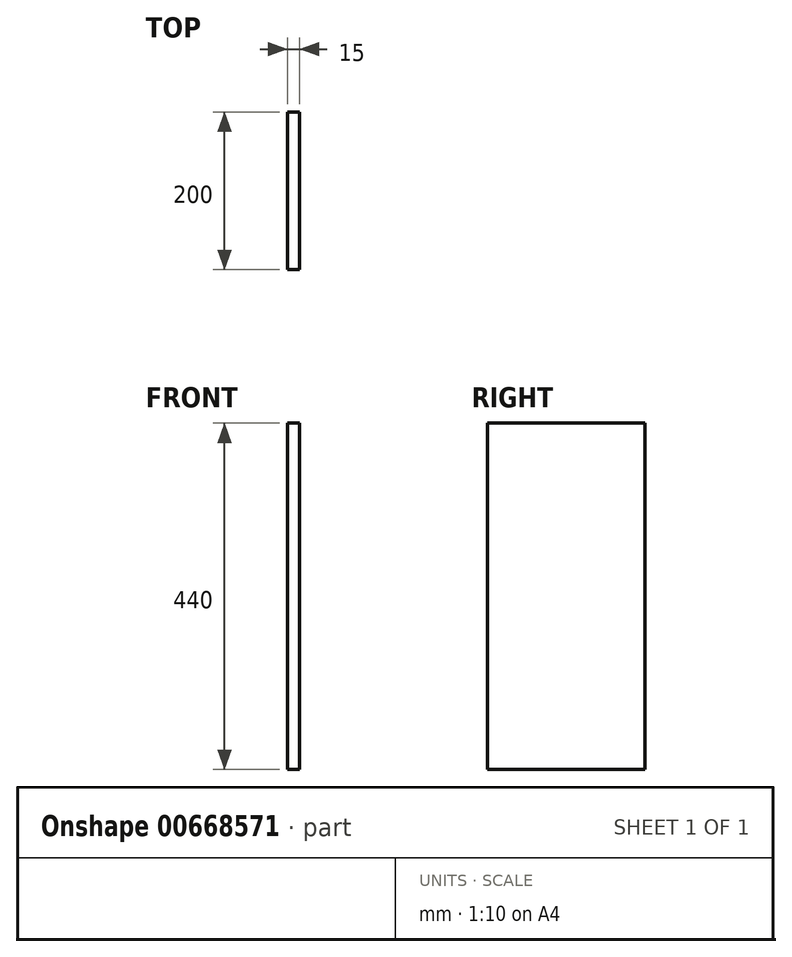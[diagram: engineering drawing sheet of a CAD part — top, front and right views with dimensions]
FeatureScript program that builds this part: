
annotation { "Feature Type Name" : "Feature", "Feature Type Description" : "" }
export const myFeature = defineFeature(function(context is Context, id is Id, definition is map)
    precondition{}
    {
        {
            var Q0;
            Q0=qCreatedBy(makeId("Right.planeOp"),FACE);
            var sketch = newSketch(context, id + "F0", { "sketchPlane" : qUnion([Q0])});
            skLineSegment(sketch, "E0.bottom", {"start": v(0, 0) * mm, "end": v(200, 0) * mm});
            skLineSegment(sketch, "E0.top", {"start": v(0, 440) * mm, "end": v(200, 440) * mm});
            skLineSegment(sketch, "E0.left", {"start": v(0, 0) * mm, "end": v(0, 440) * mm});
            skLineSegment(sketch, "E0.right", {"start": v(200, 0) * mm, "end": v(200, 440) * mm});
            skSolve(sketch);
        }
        {
            var Q0;
            Q0=makeQuery(id+"F0.imprint","IMPRINT",FACE,{"disambiguationData":[TD([[makeQuery(id+"F0.imprint","IMPRINT",EDGE,{"derivedFrom":sQuery(id+"F0.wireOp",EDGE,"E0.bottom")}),1.0]])]});
            extrude(context, id + "F1", {"entities" : qUnion([Q0]), "depth" : 15 * mm, "offsetDistance" : 25 * mm});
        }
    });
